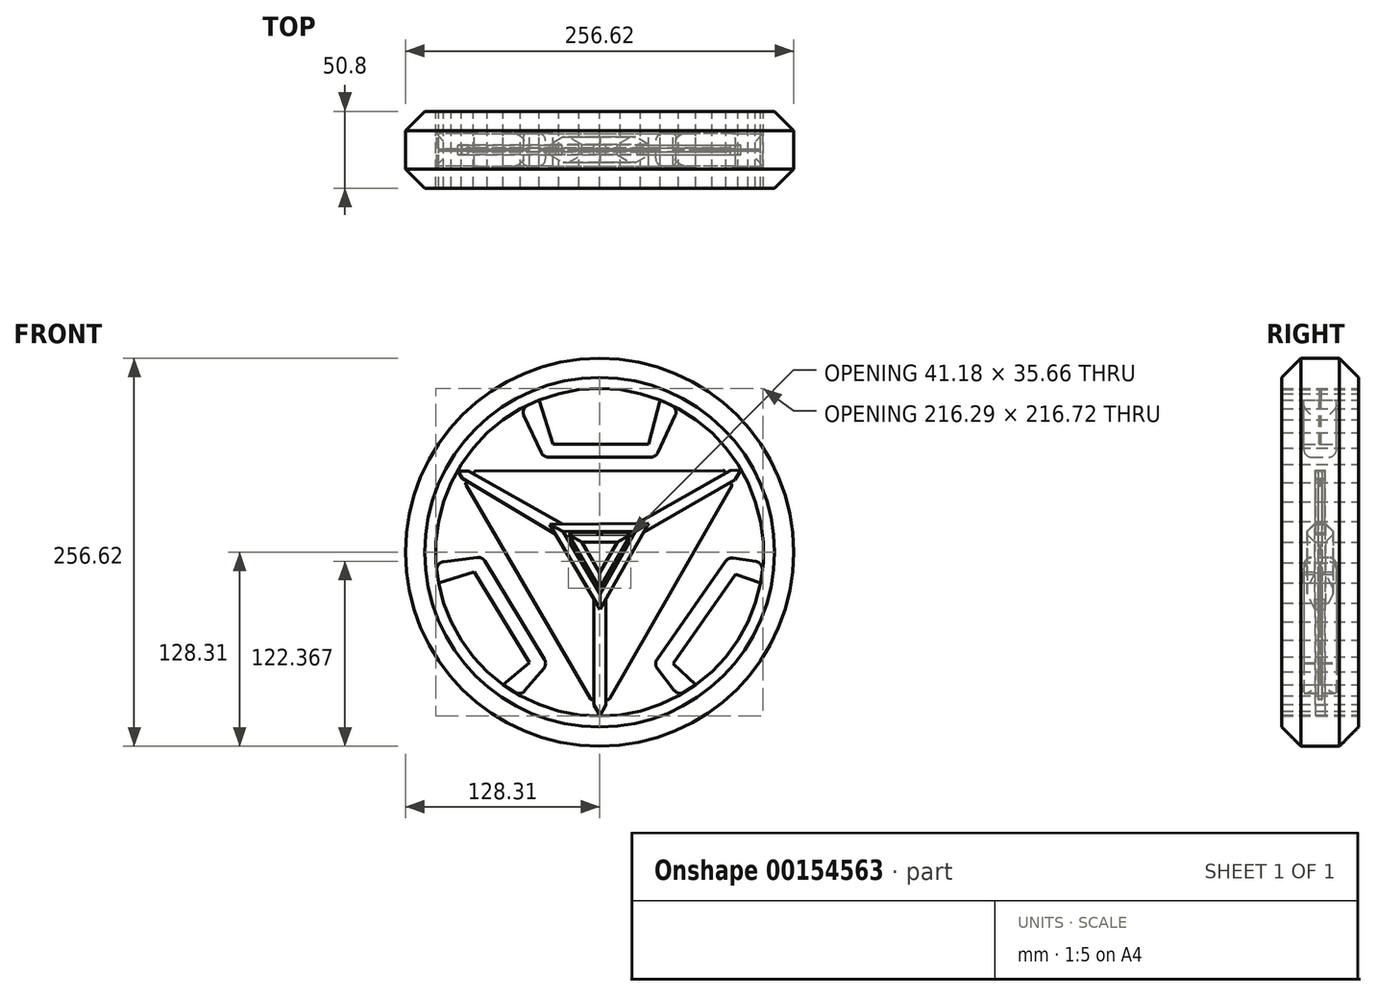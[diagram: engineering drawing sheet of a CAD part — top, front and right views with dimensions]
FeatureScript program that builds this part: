
annotation { "Feature Type Name" : "Feature", "Feature Type Description" : "" }
export const myFeature = defineFeature(function(context is Context, id is Id, definition is map)
    precondition{}
    {
        {
            var Q0;
            Q0=qCreatedBy(makeId("Front.planeOp"),FACE);
            var sketch = newSketch(context, id + "F0", { "sketchPlane" : qUnion([Q0])});
            skLineSegment(sketch, "E0.0", {"start": v(93.23, 54.18) * mm, "end": v(0.3, -107.83) * mm});
            skLineSegment(sketch, "E0.1", {"start": v(0.3, -107.83) * mm, "end": v(-93.54, 53.65) * mm});
            skLineSegment(sketch, "E0.2", {"start": v(-93.54, 53.65) * mm, "end": v(93.23, 54.18) * mm});
            skLineSegment(sketch, "E1.0", {"start": v(-32.94, 18.6) * mm, "end": v(32.57, 19.23) * mm});
            skLineSegment(sketch, "E1.1", {"start": v(32.57, 19.23) * mm, "end": v(0.36, -37.82) * mm});
            skLineSegment(sketch, "E1.2", {"start": v(0.36, -37.82) * mm, "end": v(-32.94, 18.6) * mm});
            skLineSegment(sketch, "E2", {"start": v(4.24, -30.96) * mm, "end": v(4.24, -100.97) * mm});
            skLineSegment(sketch, "E3", {"start": v(-3.69, -100.97) * mm, "end": v(-3.69, -30.96) * mm});
            skLineSegment(sketch, "E4", {"start": v(-86.27, 41.16) * mm, "end": v(-83.71, 36.75) * mm});
            skLineSegment(sketch, "E5", {"start": v(-86.58, 53.67) * mm, "end": v(-24.77, 18.68) * mm});
            skLineSegment(sketch, "E6", {"start": v(-28.9, 11.74) * mm, "end": v(-90.75, 48.87) * mm});
            skLineSegment(sketch, "E7", {"start": v(24.66, 19.15) * mm, "end": v(86.53, 54.16) * mm});
            skLineSegment(sketch, "E8", {"start": v(29.05, 12.98) * mm, "end": v(89.61, 47.87) * mm});
            skCircle(sketch, "E9.cCircle", {"center": v(0, 0) * mm, "radius": 108.36 * mm, "construction": true});
            skLineSegment(sketch, "E9.0", {"start": v(-13.58, -107.5) * mm, "end": v(0, -108.36) * mm});
            skLineSegment(sketch, "E9.1", {"start": v(-26.95, -104.96) * mm, "end": v(-13.58, -107.5) * mm});
            skLineSegment(sketch, "E9.2", {"start": v(-39.9, -100.75) * mm, "end": v(-26.95, -104.96) * mm});
            skLineSegment(sketch, "E9.3", {"start": v(-52.2, -94.96) * mm, "end": v(-39.9, -100.75) * mm});
            skLineSegment(sketch, "E9.4", {"start": v(-63.7, -87.67) * mm, "end": v(-52.2, -94.96) * mm});
            skLineSegment(sketch, "E9.5", {"start": v(-74.18, -79) * mm, "end": v(-63.7, -87.67) * mm});
            skLineSegment(sketch, "E9.6", {"start": v(-83.5, -69.07) * mm, "end": v(-74.18, -79) * mm});
            skLineSegment(sketch, "E9.7", {"start": v(-91.5, -58.06) * mm, "end": v(-83.5, -69.07) * mm});
            skLineSegment(sketch, "E9.8", {"start": v(-98.05, -46.14) * mm, "end": v(-91.5, -58.06) * mm});
            skLineSegment(sketch, "E9.9", {"start": v(-103.06, -33.49) * mm, "end": v(-98.05, -46.14) * mm});
            skLineSegment(sketch, "E9.10", {"start": v(-106.44, -20.3) * mm, "end": v(-103.06, -33.49) * mm});
            skLineSegment(sketch, "E9.11", {"start": v(-108.15, -6.8) * mm, "end": v(-106.44, -20.3) * mm});
            skLineSegment(sketch, "E9.12", {"start": v(-108.15, 6.8) * mm, "end": v(-108.15, -6.8) * mm});
            skLineSegment(sketch, "E9.13", {"start": v(-106.44, 20.3) * mm, "end": v(-108.15, 6.8) * mm});
            skLineSegment(sketch, "E9.14", {"start": v(-103.06, 33.49) * mm, "end": v(-106.44, 20.3) * mm});
            skLineSegment(sketch, "E9.15", {"start": v(-98.05, 46.14) * mm, "end": v(-103.06, 33.49) * mm});
            skLineSegment(sketch, "E9.16", {"start": v(-91.5, 58.06) * mm, "end": v(-98.05, 46.14) * mm});
            skLineSegment(sketch, "E9.17", {"start": v(-83.5, 69.07) * mm, "end": v(-91.5, 58.06) * mm});
            skLineSegment(sketch, "E9.18", {"start": v(-74.18, 79) * mm, "end": v(-83.5, 69.07) * mm});
            skLineSegment(sketch, "E9.19", {"start": v(-63.7, 87.67) * mm, "end": v(-74.18, 79) * mm});
            skLineSegment(sketch, "E9.20", {"start": v(-52.2, 94.96) * mm, "end": v(-63.7, 87.67) * mm});
            skLineSegment(sketch, "E9.21", {"start": v(-39.9, 100.75) * mm, "end": v(-52.2, 94.96) * mm});
            skLineSegment(sketch, "E9.22", {"start": v(-26.95, 104.96) * mm, "end": v(-39.9, 100.75) * mm});
            skLineSegment(sketch, "E9.23", {"start": v(-13.58, 107.5) * mm, "end": v(-26.95, 104.96) * mm});
            skLineSegment(sketch, "E9.24", {"start": v(0, 108.36) * mm, "end": v(-13.58, 107.5) * mm});
            skLineSegment(sketch, "E9.25", {"start": v(13.58, 107.5) * mm, "end": v(0, 108.36) * mm});
            skLineSegment(sketch, "E9.26", {"start": v(26.95, 104.96) * mm, "end": v(13.58, 107.5) * mm});
            skLineSegment(sketch, "E9.27", {"start": v(39.9, 100.75) * mm, "end": v(26.95, 104.96) * mm});
            skLineSegment(sketch, "E9.28", {"start": v(52.2, 94.96) * mm, "end": v(39.9, 100.75) * mm});
            skLineSegment(sketch, "E9.29", {"start": v(63.7, 87.67) * mm, "end": v(52.2, 94.96) * mm});
            skLineSegment(sketch, "E9.30", {"start": v(74.18, 79) * mm, "end": v(63.7, 87.67) * mm});
            skLineSegment(sketch, "E9.31", {"start": v(83.5, 69.07) * mm, "end": v(74.18, 79) * mm});
            skLineSegment(sketch, "E9.32", {"start": v(91.5, 58.06) * mm, "end": v(83.5, 69.07) * mm});
            skLineSegment(sketch, "E9.33", {"start": v(98.05, 46.14) * mm, "end": v(91.5, 58.06) * mm});
            skLineSegment(sketch, "E9.34", {"start": v(103.06, 33.49) * mm, "end": v(98.05, 46.14) * mm});
            skLineSegment(sketch, "E9.35", {"start": v(106.44, 20.3) * mm, "end": v(103.06, 33.49) * mm});
            skLineSegment(sketch, "E9.36", {"start": v(108.15, 6.8) * mm, "end": v(106.44, 20.3) * mm});
            skLineSegment(sketch, "E9.37", {"start": v(108.15, -6.8) * mm, "end": v(108.15, 6.8) * mm});
            skLineSegment(sketch, "E9.38", {"start": v(106.44, -20.3) * mm, "end": v(108.15, -6.8) * mm});
            skLineSegment(sketch, "E9.39", {"start": v(103.06, -33.49) * mm, "end": v(106.44, -20.3) * mm});
            skLineSegment(sketch, "E9.40", {"start": v(98.05, -46.14) * mm, "end": v(103.06, -33.49) * mm});
            skLineSegment(sketch, "E9.41", {"start": v(91.5, -58.06) * mm, "end": v(98.05, -46.14) * mm});
            skLineSegment(sketch, "E9.42", {"start": v(83.5, -69.07) * mm, "end": v(91.5, -58.06) * mm});
            skLineSegment(sketch, "E9.43", {"start": v(74.18, -79) * mm, "end": v(83.5, -69.07) * mm});
            skLineSegment(sketch, "E9.44", {"start": v(63.7, -87.67) * mm, "end": v(74.18, -79) * mm});
            skLineSegment(sketch, "E9.45", {"start": v(52.2, -94.96) * mm, "end": v(63.7, -87.67) * mm});
            skLineSegment(sketch, "E9.46", {"start": v(39.9, -100.75) * mm, "end": v(52.2, -94.96) * mm});
            skLineSegment(sketch, "E9.47", {"start": v(26.95, -104.96) * mm, "end": v(39.9, -100.75) * mm});
            skLineSegment(sketch, "E9.48", {"start": v(13.58, -107.5) * mm, "end": v(26.95, -104.96) * mm});
            skLineSegment(sketch, "E9.49", {"start": v(0, -108.36) * mm, "end": v(13.58, -107.5) * mm});
            skLineSegment(sketch, "E10.0", {"start": v(0, -13.61) * mm, "end": v(-11.79, 6.8) * mm});
            skLineSegment(sketch, "E10.1", {"start": v(-11.79, 6.8) * mm, "end": v(11.79, 6.8) * mm});
            skLineSegment(sketch, "E10.2", {"start": v(11.79, 6.8) * mm, "end": v(0, -13.61) * mm});
            skLineSegment(sketch, "E11", {"start": v(89.74, -14.56) * mm, "end": v(48.6, -73.49) * mm});
            skLineSegment(sketch, "E12", {"start": v(85.15, -3.4) * mm, "end": v(35.89, -73.94) * mm});
            skLineSegment(sketch, "E13", {"start": v(-77.64, -2.95) * mm, "end": v(-34.5, -73.94) * mm});
            skLineSegment(sketch, "E14", {"start": v(-82.82, -12.87) * mm, "end": v(-46.16, -72.86) * mm});
            skLineSegment(sketch, "E15", {"start": v(-37.12, 62.9) * mm, "end": v(37.12, 62.9) * mm});
            skLineSegment(sketch, "E16", {"start": v(-30.7, 71.54) * mm, "end": v(32.57, 71.54) * mm});
            skLineSegment(sketch, "E17", {"start": v(35.89, -73.94) * mm, "end": v(52.2, -94.96) * mm});
            skLineSegment(sketch, "E18", {"start": v(48.6, -73.49) * mm, "end": v(63.7, -87.67) * mm});
            skLineSegment(sketch, "E19", {"start": v(85.15, -3.4) * mm, "end": v(108.15, -6.8) * mm});
            skLineSegment(sketch, "E20", {"start": v(89.74, -14.56) * mm, "end": v(106.44, -20.3) * mm});
            skLineSegment(sketch, "E21", {"start": v(-82.82, -12.87) * mm, "end": v(-106.44, -20.3) * mm});
            skLineSegment(sketch, "E22", {"start": v(-77.64, -2.95) * mm, "end": v(-108.15, -6.8) * mm});
            skLineSegment(sketch, "E23", {"start": v(-46.16, -72.86) * mm, "end": v(-63.7, -87.67) * mm});
            skLineSegment(sketch, "E24", {"start": v(-34.5, -73.94) * mm, "end": v(-52.2, -94.96) * mm});
            skLineSegment(sketch, "E25", {"start": v(-30.7, 71.54) * mm, "end": v(-39.9, 100.75) * mm});
            skLineSegment(sketch, "E26", {"start": v(32.57, 71.54) * mm, "end": v(39.9, 100.75) * mm});
            skLineSegment(sketch, "E27", {"start": v(37.12, 62.9) * mm, "end": v(52.2, 94.96) * mm});
            skLineSegment(sketch, "E28", {"start": v(-37.12, 62.9) * mm, "end": v(-52.2, 94.96) * mm});
            skCircle(sketch, "E29.0", {"center": v(0, 0) * mm, "radius": 128.3 * mm});
            skSolve(sketch);
        }
        {
            var Q0;
            Q0=makeQuery(id+"F0.imprint","IMPRINT",FACE,{"disambiguationData":[TD([[makeQuery(id+"F0.imprint","IMPRINT",EDGE,{"derivedFrom":sQuery(id+"F0.wireOp",EDGE,"E9.0")}),-1.0]])]});
            extrude(context, id + "F1", {"entities" : qUnion([Q0]), "endBound" : BoundingType.SYMMETRIC, "depth" : 50.8 * mm});
        }
        {
            var Q0;
            {var subQ0=sQuery(id+"F0.wireOp",EDGE,"E5");Q0=makeQuery(id+"F0.imprint","IMPRINT",FACE,{"disambiguationData":[TD([[makeQuery(id+"F0.imprint","IMPRINT",EDGE,{"derivedFrom":subQ0}),1.0]])]});}
            var Q1;
            {var subQ0=sQuery(id+"F0.wireOp",EDGE,"E3");Q1=makeQuery(id+"F0.imprint","IMPRINT",FACE,{"disambiguationData":[TD([[makeQuery(id+"F0.imprint","IMPRINT",EDGE,{"derivedFrom":subQ0}),1.0]])]});}
            var Q2;
            {var subQ0=sQuery(id+"F0.wireOp",EDGE,"E2");Q2=makeQuery(id+"F0.imprint","IMPRINT",FACE,{"disambiguationData":[TD([[makeQuery(id+"F0.imprint","IMPRINT",EDGE,{"derivedFrom":subQ0}),1.0]])]});}
            extrude(context, id + "F2", {"entities" : qUnion([Q0, Q1, Q2]), "endBound" : BoundingType.SYMMETRIC, "depth" : 2.54 * mm});
        }
        {
            var Q0;
            {var subQ7=sQuery(id+"F0.wireOp",EDGE,"E5");Q0=makeQuery(id+"F0.imprint","IMPRINT",FACE,{"disambiguationData":[TD([[makeQuery(id+"F0.imprint","IMPRINT",EDGE,{"derivedFrom":subQ7}),-1.0]])]});}
            var Q1;
            {var subQ4=sQuery(id+"F0.wireOp",EDGE,"E7");Q1=makeQuery(id+"F0.imprint","IMPRINT",FACE,{"disambiguationData":[TD([[makeQuery(id+"F0.imprint","IMPRINT",EDGE,{"derivedFrom":subQ4}),-1.0]])]});}
            var Q2;
            {var subQ3=sQuery(id+"F0.wireOp",EDGE,"E2");Q2=makeQuery(id+"F0.imprint","IMPRINT",FACE,{"disambiguationData":[TD([[makeQuery(id+"F0.imprint","IMPRINT",EDGE,{"derivedFrom":subQ3}),-1.0]])]});}
            extrude(context, id + "F3", {"entities" : qUnion([Q0, Q1, Q2]), "endBound" : BoundingType.SYMMETRIC, "depth" : 6.35 * mm});
        }
        {
            var Q0;
            Q0=makeQuery(id+"F0.imprint","IMPRINT",FACE,{"disambiguationData":[TD([[makeQuery(id+"F0.imprint","IMPRINT",EDGE,{"derivedFrom":sQuery(id+"F0.wireOp",EDGE,"E10.0")}),-1.0]])]});
            var Q1;
            {var subQ0=sQuery(id+"F0.wireOp",EDGE,"E4");Q1=makeQuery(id+"F0.imprint","IMPRINT",FACE,{"disambiguationData":[TD([[makeQuery(id+"F0.imprint","IMPRINT",EDGE,{"derivedFrom":subQ0}),-1.0]])]});}
            var Q2;
            Q2=makeQuery(id+"F0.imprint","IMPRINT",FACE,{"disambiguationData":[TD([[makeQuery(id+"F0.imprint","IMPRINT",EDGE,{"derivedFrom":sQuery(id+"F0.wireOp",EDGE,"E9.22")}),1.0]])]});
            var Q3;
            Q3=makeQuery(id+"F0.imprint","IMPRINT",FACE,{"disambiguationData":[TD([[makeQuery(id+"F0.imprint","IMPRINT",EDGE,{"derivedFrom":sQuery(id+"F0.wireOp",EDGE,"E9.39")}),1.0]])]});
            var Q4;
            Q4=makeQuery(id+"F0.imprint","IMPRINT",FACE,{"disambiguationData":[TD([[makeQuery(id+"F0.imprint","IMPRINT",EDGE,{"derivedFrom":sQuery(id+"F0.wireOp",EDGE,"E9.5")}),1.0]])]});
            extrude(context, id + "F4", {"entities" : qUnion([Q0, Q1, Q2, Q3, Q4]), "endBound" : BoundingType.SYMMETRIC, "depth" : 1.27 * mm});
        }
        {
            var Q0;
            Q0=makeQuery(id+"F0.imprint","IMPRINT",FACE,{"disambiguationData":[TD([[makeQuery(id+"F0.imprint","IMPRINT",EDGE,{"derivedFrom":sQuery(id+"F0.wireOp",EDGE,"E9.21")}),1.0]])]});
            var Q1;
            Q1=makeQuery(id+"F0.imprint","IMPRINT",FACE,{"disambiguationData":[TD([[makeQuery(id+"F0.imprint","IMPRINT",EDGE,{"derivedFrom":sQuery(id+"F0.wireOp",EDGE,"E9.4")}),1.0]])]});
            var Q2;
            Q2=makeQuery(id+"F0.imprint","IMPRINT",FACE,{"disambiguationData":[TD([[makeQuery(id+"F0.imprint","IMPRINT",EDGE,{"derivedFrom":sQuery(id+"F0.wireOp",EDGE,"E9.38")}),1.0]])]});
            extrude(context, id + "F5", {"entities" : qUnion([Q0, Q1, Q2]), "endBound" : BoundingType.SYMMETRIC, "depth" : 21.59 * mm});
        }
        {
            var Q0;
            Q0=makeQuery(id+"F0.imprint","IMPRINT",FACE,{"disambiguationData":[TD([[makeQuery(id+"F0.imprint","IMPRINT",EDGE,{"derivedFrom":sQuery(id+"F0.wireOp",EDGE,"E10.0")}),1.0]])]});
            extrude(context, id + "F6", {"entities" : qUnion([Q0]), "endBound" : BoundingType.SYMMETRIC, "depth" : 17.02 * mm});
        }
        {
            var Q0;
            Q0=makeQuery(id+"F1.opExtrude","CAP_EDGE",EDGE,{"disambiguationData":[OSD([sQuery(id+"F0.wireOp",EDGE,"E29.0")])],"isStart":false});
            var Q1;
            Q1=makeQuery(id+"F1.opExtrude","CAP_EDGE",EDGE,{"disambiguationData":[OSD([sQuery(id+"F0.wireOp",EDGE,"E29.0")])],"isStart":true});
            chamfer(context, id + "F7", {"entities" : qUnion([Q0, Q1]), "width" : 12.7 * mm, "tangentPropagation" : true});
        }
        {
            var Q0;
            Q0=makeQuery(id+"F5.opExtrude","SWEPT_FACE",FACE,{"disambiguationData":[OSD([sQuery(id+"F0.wireOp",EDGE,"E15")])]});
            var Q1;
            Q1=makeQuery(id+"F5.opExtrude","SWEPT_FACE",FACE,{"disambiguationData":[OSD([sQuery(id+"F0.wireOp",EDGE,"E28")])]});
            var Q2;
            Q2=makeQuery(id+"F5.opExtrude","SWEPT_FACE",FACE,{"disambiguationData":[OSD([sQuery(id+"F0.wireOp",EDGE,"E27")])]});
            var Q3;
            Q3=makeQuery(id+"F5.opExtrude","SWEPT_FACE",FACE,{"disambiguationData":[OSD([sQuery(id+"F0.wireOp",EDGE,"E13")])]});
            var Q4;
            Q4=makeQuery(id+"F5.opExtrude","SWEPT_FACE",FACE,{"disambiguationData":[OSD([sQuery(id+"F0.wireOp",EDGE,"E24")])]});
            var Q5;
            Q5=makeQuery(id+"F5.opExtrude","SWEPT_FACE",FACE,{"disambiguationData":[OSD([sQuery(id+"F0.wireOp",EDGE,"E22")])]});
            var Q6;
            Q6=makeQuery(id+"F5.opExtrude","SWEPT_FACE",FACE,{"disambiguationData":[OSD([sQuery(id+"F0.wireOp",EDGE,"E12")])]});
            var Q7;
            Q7=makeQuery(id+"F5.opExtrude","SWEPT_FACE",FACE,{"disambiguationData":[OSD([sQuery(id+"F0.wireOp",EDGE,"E19")])]});
            var Q8;
            Q8=makeQuery(id+"F5.opExtrude","SWEPT_FACE",FACE,{"disambiguationData":[OSD([sQuery(id+"F0.wireOp",EDGE,"E17")])]});
            fillet(context, id + "F8", {"entities" : qUnion([Q0, Q1, Q2, Q3, Q4, Q5, Q6, Q7, Q8]), "radius" : 5.08 * mm, "tangentPropagation" : true, "allowEdgeOverflow" : false});
        }
        {
            var Q0;
            Q0=makeQuery(id+"F2.opExtrude","SWEPT_FACE",FACE,{"disambiguationData":[OSD([sQuery(id+"F0.wireOp",EDGE,"E0.0")])]});
            var Q1;
            Q1=makeQuery(id+"F2.opExtrude","SWEPT_FACE",FACE,{"disambiguationData":[OSD([sQuery(id+"F0.wireOp",EDGE,"E0.2")])]});
            var Q2;
            Q2=makeQuery(id+"F2.opExtrude","SWEPT_FACE",FACE,{"disambiguationData":[OSD([sQuery(id+"F0.wireOp",EDGE,"E0.1"),sQuery(id+"F0.wireOp",EDGE,"E4")])]});
            fillet(context, id + "F9", {"entities" : qUnion([Q0, Q1, Q2]), "radius" : 1.27 * mm, "tangentPropagation" : true, "allowEdgeOverflow" : false});
        }
        {
            var Q0;
            Q0=makeQuery(id+"F6.opExtrude","CAP_FACE",FACE,{"disambiguationData":[OSD([sQuery(id+"F0.wireOp",EDGE,"E1.0"),sQuery(id+"F0.wireOp",EDGE,"E1.1"),sQuery(id+"F0.wireOp",EDGE,"E1.2"),sQuery(id+"F0.wireOp",EDGE,"E10.0"),sQuery(id+"F0.wireOp",EDGE,"E10.1"),sQuery(id+"F0.wireOp",EDGE,"E10.2")])],"isStart":false});
            var Q1;
            Q1=makeQuery(id+"F6.opExtrude","CAP_FACE",FACE,{"disambiguationData":[OSD([sQuery(id+"F0.wireOp",EDGE,"E1.0"),sQuery(id+"F0.wireOp",EDGE,"E1.1"),sQuery(id+"F0.wireOp",EDGE,"E1.2"),sQuery(id+"F0.wireOp",EDGE,"E10.0"),sQuery(id+"F0.wireOp",EDGE,"E10.1"),sQuery(id+"F0.wireOp",EDGE,"E10.2")])],"isStart":true});
            chamfer(context, id + "F10", {"entities" : qUnion([Q0, Q1]), "width" : 5.08 * mm, "tangentPropagation" : true});
        }
    });
